# Revit family: Хомут
name_source: partatom
category: Арматура трубопроводов
revit_build: Autodesk Revit 2017 (Build: 20171027_0315(x64)
units: mm (PartAtom-declared; Revit-internal decimal feet)

## family parameters
Всегда вертикально = Да
На основе рабочей плоскости = Нет
Общий = Нет
При загрузке вырезать с полостями = Нет
Размер круглого соединителя = Использовать радиус
Тип детали = Вставляется

## types (16) — shared parameters
ADSK_Единица измерения = шт
ADSK_Завод-изготовитель = Stout
ADSK_Наименование = Хомут сантехнический с резинкой и гайкой
S1 = 3 мм
Группа модели = Хомут сантехнический с резинкой и гайкой
Изготовитель = Stout
Материал полимера = Фильтр_Черный
Материал фитинга = РВК_Полипропилен PPR
Разработчик = ООО ПРОРУБИМ
Разработчик (телефон) = +7(495)649-85-43
Разработчик модели (URL) = http://prorubim.com
zero-valued in all types: ADSK_Масса

## per-type parameters (varying)
| type | ADSK_Код изделия | B | DN | H | L | R | R+s | S | URL | t_резиночки |
| DN150 | PCNT150 | 25 мм | 150 мм | 103 мм | 227 мм | 75 мм | 77 мм | 2 мм | https://www.stout.ru | 84 мм |
| DN125 | PCNT125 | 25 мм | 125 мм | 90 мм | 199 мм | 63 мм | 65 мм | 2 мм | https://www.stout.ru | 72 мм |
| DN100 | PCNT100 | 20 мм | 100 мм | 77 мм | 173 мм | 50 мм | 52 мм | 2 мм | https://www.stout.ru | 59 мм |
| DN90 | PCNT090 | 20 мм | 90 мм | 75 мм | 160 мм | 45 мм | 47 мм | 2 мм | https://www.stout.ru | 55 мм |
| DN80 | PCNT080 | 20 мм | 80 мм | 64 мм | 147 мм | 40 мм | 42 мм | 2 мм |  | 48 мм |
| DN70 | PCNT070 | 20 мм | 70 мм | 58 мм | 134 мм | 35 мм | 37 мм | 2 мм | https://www.stout.ru | 43 мм |
| DN65 | PCNT065 | 20 мм | 65 мм | 58 мм | 134 мм | 33 мм | 34 мм | 2 мм | https://www.stout.ru | 41 мм |
| DN50 | PCNT050 | 20 мм | 50 мм | 49 мм | 112 мм | 25 мм | 27 мм | 2 мм | https://www.stout.ru | 33 мм |
| DN45 | PCNT045 | 20 мм | 45 мм | 47 мм | 110 мм | 23 мм | 24 мм | 1 мм | https://www.stout.ru | 30 мм |
| DN40 | PCNT040 | 20 мм | 40 мм | 43 мм | 99 мм | 20 мм | 21 мм | 1 мм | https://www.stout.ru | 27 мм |
| DN32 | PCNT032 | 20 мм | 32 мм | 39 мм | 92 мм | 16 мм | 17 мм | 1 мм | https://www.stout.ru | 23 мм |
| DN25 | PCNT025 | 20 мм | 25 мм | 35 мм | 77 мм | 13 мм | 14 мм | 1 мм | https://www.stout.ru | 20 мм |
| DN20 | PCNT020 | 20 мм | 20 мм | 31 мм | 69 мм | 10 мм | 11 мм | 1 мм | https://www.stout.ru | 17 мм |
| DN15 | PCNT015 | 20 мм | 15 мм | 28 мм | 63 мм | 8 мм | 9 мм | 1 мм | https://www.stout.ru | 14 мм |
| DN10 | PCNT010 | 20 мм | 10 мм | 26 мм | 59 мм | 5 мм | 6 мм | 1 мм | https://www.stout.ru | 12 мм |
| DN8 | PCNT008 | 20 мм | 8 мм | 22 мм | 51 мм | 4 мм | 5 мм | 1 мм | https://www.stout.ru | 10 мм |

note: column(s) folded — value = type name in every type: ADSK_Обозначение
